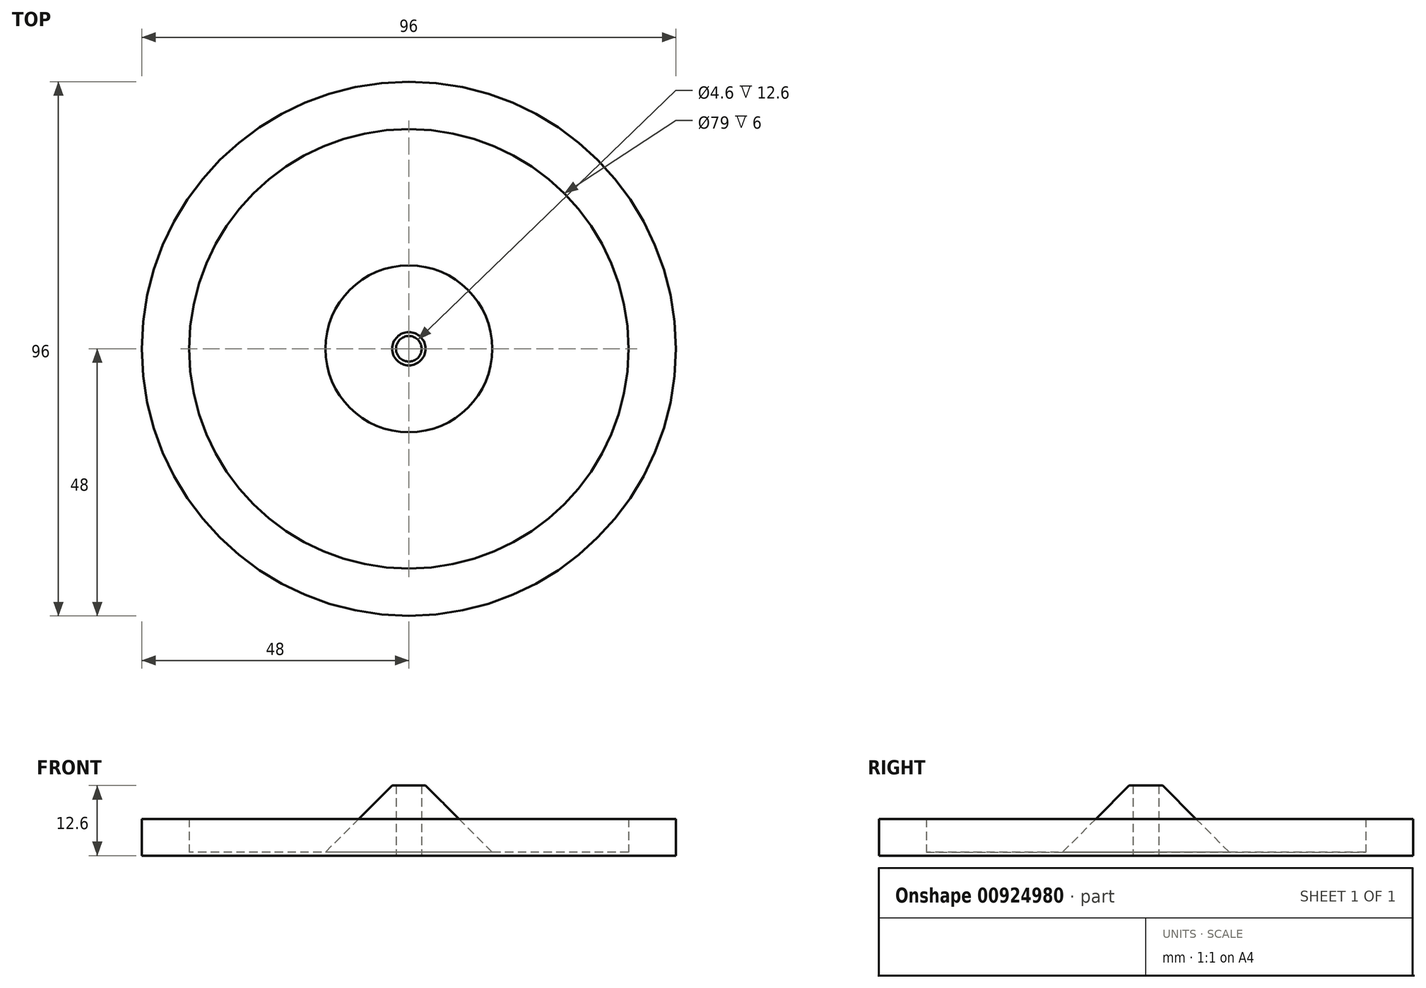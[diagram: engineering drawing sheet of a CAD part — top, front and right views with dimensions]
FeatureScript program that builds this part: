
annotation { "Feature Type Name" : "Feature", "Feature Type Description" : "" }
export const myFeature = defineFeature(function(context is Context, id is Id, definition is map)
    precondition{}
    {
        {
            var Q0;
            Q0=qCreatedBy(makeId("Top.planeOp"),FACE);
            var sketch = newSketch(context, id + "F0", { "sketchPlane" : qUnion([Q0])});
            skCircle(sketch, "E0", {"center": v(0, 0) * mm, "radius": 39.5 * mm});
            skCircle(sketch, "E1", {"center": v(0, 0) * mm, "radius": 48 * mm});
            skCircle(sketch, "E2", {"center": v(0, 0) * mm, "radius": 2.3 * mm});
            skCircle(sketch, "E3", {"center": v(0, 0) * mm, "radius": 15 * mm});
            skSolve(sketch);
        }
        {
            var Q0;
            Q0=makeQuery(id+"F0.imprint","IMPRINT",FACE,{"disambiguationData":[TD([[makeQuery(id+"F0.imprint","IMPRINT",EDGE,{"derivedFrom":sQuery(id+"F0.wireOp",EDGE,"E2")}),-1.0]])]});
            extrude(context, id + "F1", {"entities" : qUnion([Q0]), "depth" : 12 * mm, "offsetDistance" : 25 * mm});
        }
        {
            var Q0;
            Q0=qSketchRegion(id+"F0",true);
            var Q1;
            Q1=makeQuery(id+"F0.imprint","IMPRINT",FACE,{"disambiguationData":[TD([[makeQuery(id+"F0.imprint","IMPRINT",EDGE,{"derivedFrom":sQuery(id+"F0.wireOp",EDGE,"E0")}),1.0]])]});
            var Q2;
            Q2=makeQuery(id+"F0.imprint","IMPRINT",FACE,{"disambiguationData":[TD([[makeQuery(id+"F0.imprint","IMPRINT",EDGE,{"derivedFrom":sQuery(id+"F0.wireOp",EDGE,"E2")}),-1.0]])]});
            extrude(context, id + "F2", {"entities" : qUnion([Q0, Q1, Q2]), "operationType" : NewBodyOperationType.ADD, "oppositeDirection" : true, "depth" : 0.6 * mm, "offsetDistance" : 25 * mm});
        }
        {
            var Q0;
            Q0=makeQuery(id+"F1.opExtrude","CAP_EDGE",EDGE,{"disambiguationData":[OSD([sQuery(id+"F0.wireOp",EDGE,"E3")])],"isStart":false});
            chamfer(context, id + "F3", {"entities" : qUnion([Q0]), "width" : 12 * mm, "tangentPropagation" : true});
        }
        {
            var Q0;
            Q0=makeQuery(id+"F0.imprint","IMPRINT",FACE,{"disambiguationData":[TD([[makeQuery(id+"F0.imprint","IMPRINT",EDGE,{"derivedFrom":sQuery(id+"F0.wireOp",EDGE,"E0")}),-1.0]])]});
            extrude(context, id + "F4", {"entities" : qUnion([Q0]), "operationType" : NewBodyOperationType.ADD, "depth" : 6 * mm, "offsetDistance" : 25 * mm});
        }
    });
